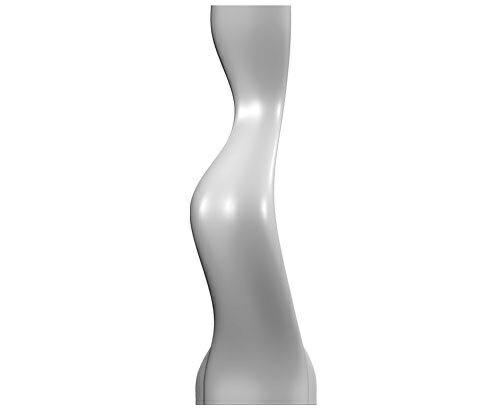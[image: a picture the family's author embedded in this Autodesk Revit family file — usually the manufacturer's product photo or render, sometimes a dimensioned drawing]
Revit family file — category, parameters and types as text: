
# Revit family: CITY ALPHABET litera „I”
name_source: partatom
category: Meble
revit_build: Autodesk Revit 2018 (Build: 20190510_1515(x64)
units: mm (PartAtom-declared; Revit-internal decimal feet)

## family parameters
Numer OmniClass = 23.40.10.11.14
Obiekt nadrzędny = Powierzchnia
Punkt obliczania pomieszczeń = Nie
Tnij formami wycięć po wczytaniu = Nie
Tytuł OmniClass = Exterior Seating
Współdzielony = Nie

## types (1)
- CITY ALPHABET litera „I”
    Domyślna rzędna = 1219 mm
    Długość = 760 mm
    IfcExportAs = IfcFurnishingElement
    Komentarze do typu = Ławka
    Materiał - informacja = Szeroki wybór kolorów wg palety RAL. Istnieje również możliwość specjalnego wykonania
kolorystycznego na indywidualne zapytanie klienta.
    Model = CITY ALPHABET litera „I”
    Obraz typu = I.jpg
    Producent = Astrini Design
    Szerokość = 2400 mm
    Temepratura użytkowania = -40°C do 80°C, ( -40°F do 176°F )
    URL = http://astrini-design.pl
    Waga (szacunkowo) = 35.00 kg
    Waga po wypełnieniu (szacunkowo) = 85.00 kg
    Wysokość = 590 mm  [stored 1.9357 ft]

note: [stored X ft] marks values corroborated as IEEE doubles in the binary element streams (Revit-internal decimal feet)
